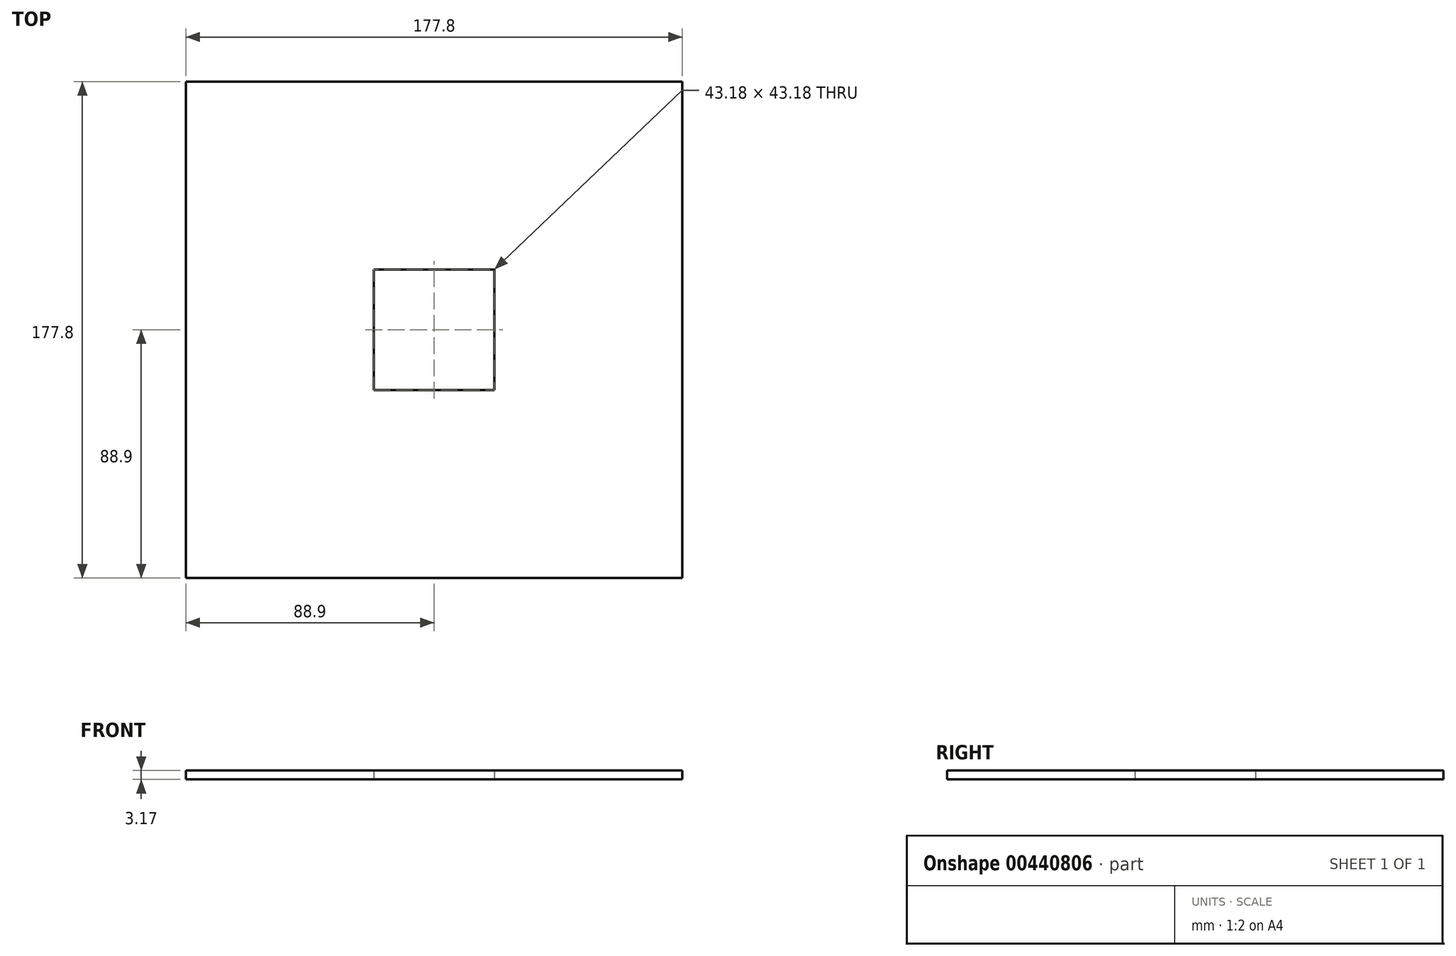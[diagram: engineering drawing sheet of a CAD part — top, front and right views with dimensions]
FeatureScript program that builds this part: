
annotation { "Feature Type Name" : "Feature", "Feature Type Description" : "" }
export const myFeature = defineFeature(function(context is Context, id is Id, definition is map)
    precondition{}
    {
        {
            var Q0;
            Q0=qCreatedBy(makeId("Top.planeOp"),FACE);
            var sketch = newSketch(context, id + "F0", { "sketchPlane" : qUnion([Q0])});
            skLineSegment(sketch, "E0.bottom", {"start": v(88.9, 88.9) * mm, "end": v(-88.9, 88.9) * mm});
            skLineSegment(sketch, "E0.top", {"start": v(88.9, -88.9) * mm, "end": v(-88.9, -88.9) * mm});
            skLineSegment(sketch, "E0.left", {"start": v(88.9, 88.9) * mm, "end": v(88.9, -88.9) * mm});
            skLineSegment(sketch, "E0.right", {"start": v(-88.9, 88.9) * mm, "end": v(-88.9, -88.9) * mm});
            skLineSegment(sketch, "E1.bottom", {"start": v(21.59, 21.6) * mm, "end": v(-21.6, 21.6) * mm});
            skLineSegment(sketch, "E1.top", {"start": v(21.6, -21.6) * mm, "end": v(-21.59, -21.6) * mm});
            skLineSegment(sketch, "E1.left", {"start": v(21.59, 21.6) * mm, "end": v(21.6, -21.6) * mm});
            skLineSegment(sketch, "E1.right", {"start": v(-21.6, 21.6) * mm, "end": v(-21.59, -21.6) * mm});
            skPoint(sketch, "E1.middle", {"position": v(0, 0) * mm});
            skLineSegment(sketch, "E2.bottom", {"start": v(-14.24, -21.6) * mm, "end": v(12.87, -21.6) * mm});
            skLineSegment(sketch, "E2.top", {"start": v(-14.24, -88.9) * mm, "end": v(12.87, -88.9) * mm});
            skLineSegment(sketch, "E2.left", {"start": v(-14.24, -21.6) * mm, "end": v(-14.24, -88.9) * mm});
            skLineSegment(sketch, "E2.right", {"start": v(12.87, -21.6) * mm, "end": v(12.87, -88.9) * mm});
            skSolve(sketch);
        }
        {
            var Q0;
            Q0=qSketchRegion(id+"F0",true);
            extrude(context, id + "F1", {"entities" : qUnion([Q0]), "depth" : 3.17 * mm});
        }
    });
